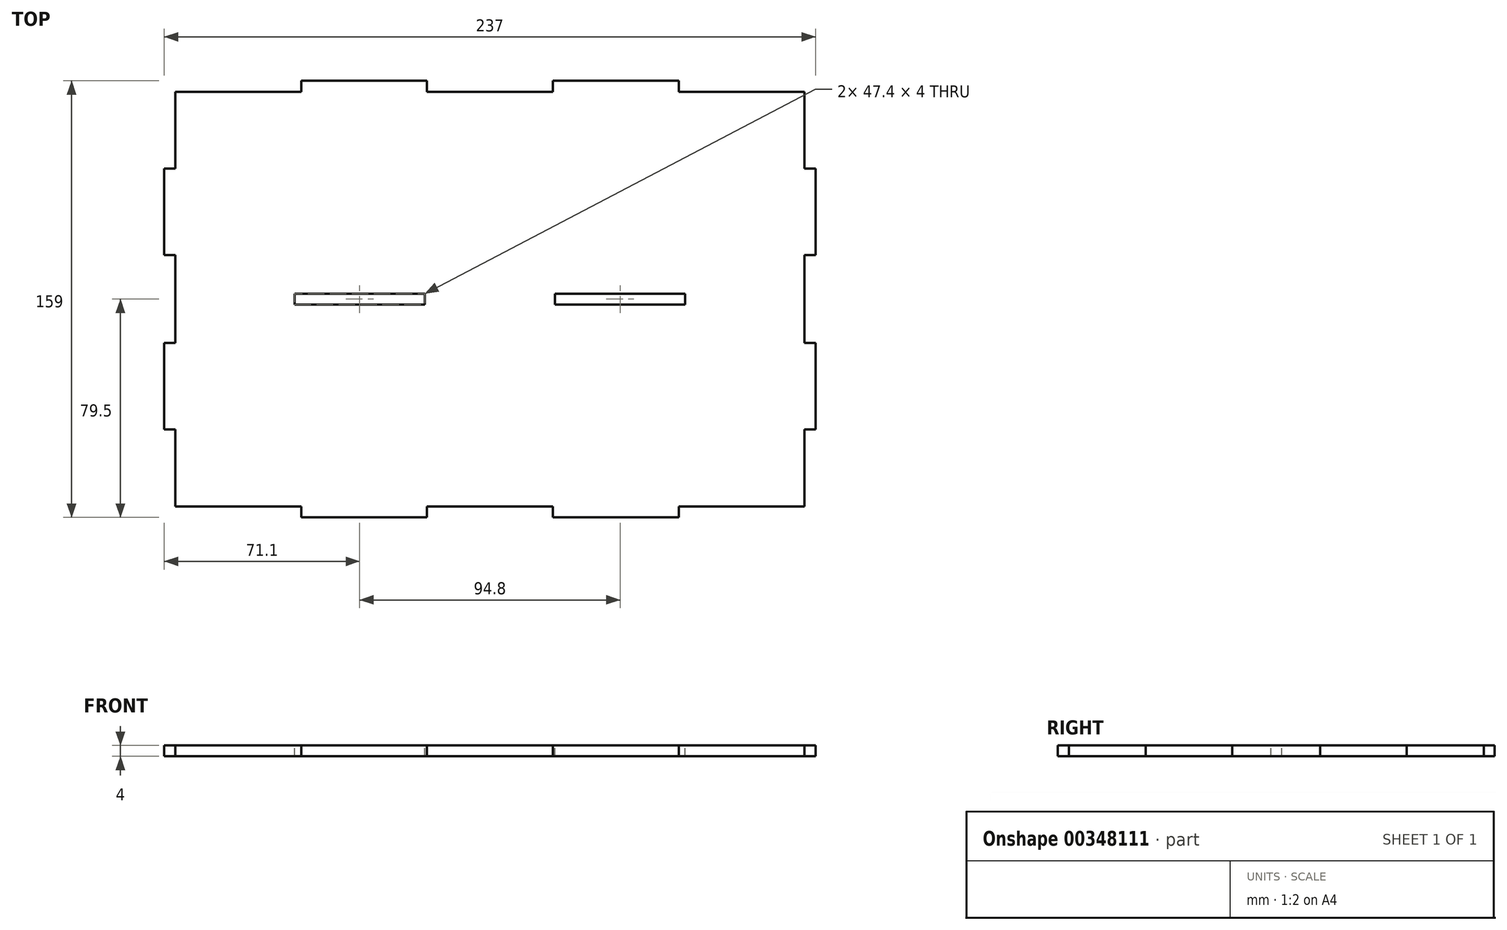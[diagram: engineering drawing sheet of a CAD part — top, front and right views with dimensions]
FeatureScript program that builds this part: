
annotation { "Feature Type Name" : "Feature", "Feature Type Description" : "" }
export const myFeature = defineFeature(function(context is Context, id is Id, definition is map)
    precondition{}
    {
        {
            var Q0;
            Q0=qCreatedBy(makeId("Top.planeOp"),FACE);
            var sketch = newSketch(context, id + "F0", { "sketchPlane" : qUnion([Q0])});
            skLineSegment(sketch, "E0.bottom", {"start": v(0, 0) * mm, "end": v(237, 0) * mm});
            skLineSegment(sketch, "E0.top", {"start": v(0, 159) * mm, "end": v(237, 159) * mm});
            skLineSegment(sketch, "E0.left", {"start": v(0, 0) * mm, "end": v(0, 159) * mm});
            skLineSegment(sketch, "E0.right", {"start": v(237, 0) * mm, "end": v(237, 159) * mm});
            skSolve(sketch);
        }
        {
            var Q0;
            Q0=makeQuery(id+"F0.imprint","IMPRINT",FACE,{"disambiguationData":[TD([[makeQuery(id+"F0.imprint","IMPRINT",EDGE,{"derivedFrom":sQuery(id+"F0.wireOp",EDGE,"E0.bottom")}),1.0]])]});
            extrude(context, id + "F1", {"entities" : qUnion([Q0]), "depth" : 4 * mm});
        }
        {
            var Q0;
            Q0=makeQuery(id+"F1.opExtrude","CAP_FACE",FACE,{"disambiguationData":[OSD([sQuery(id+"F0.wireOp",EDGE,"E0.bottom"),sQuery(id+"F0.wireOp",EDGE,"E0.top"),sQuery(id+"F0.wireOp",EDGE,"E0.left"),sQuery(id+"F0.wireOp",EDGE,"E0.right")])],"isStart":false});
            var sketch = newSketch(context, id + "F2", { "sketchPlane" : qUnion([Q0])});
            skLineSegment(sketch, "E1.0", {"start": v(4, 155) * mm, "end": v(233, 155) * mm, "construction": true});
            skLineSegment(sketch, "E1.1", {"start": v(4, 4) * mm, "end": v(4, 155) * mm, "construction": true});
            skLineSegment(sketch, "E1.2", {"start": v(4, 4) * mm, "end": v(233, 4) * mm, "construction": true});
            skLineSegment(sketch, "E1.3", {"start": v(233, 4) * mm, "end": v(233, 155) * mm, "construction": true});
            skLineSegment(sketch, "E2", {"start": v(4, 79.5) * mm, "end": v(233, 79.5) * mm, "construction": true});
            skLineSegment(sketch, "E3.bottom", {"start": v(4, 32) * mm, "end": v(0, 32) * mm});
            skLineSegment(sketch, "E3.top", {"start": v(4, 0) * mm, "end": v(0, 0) * mm});
            skLineSegment(sketch, "E3.left", {"start": v(4, 32) * mm, "end": v(4, 0) * mm});
            skLineSegment(sketch, "E3.right", {"start": v(0, 32) * mm, "end": v(0, 0) * mm});
            skLineSegment(sketch, "E4.bottom", {"start": v(4, 79.5) * mm, "end": v(0, 79.5) * mm});
            skLineSegment(sketch, "E4.top", {"start": v(4, 63.5) * mm, "end": v(0, 63.5) * mm});
            skLineSegment(sketch, "E4.left", {"start": v(4, 79.5) * mm, "end": v(4, 63.5) * mm});
            skLineSegment(sketch, "E4.right", {"start": v(0, 79.5) * mm, "end": v(0, 63.5) * mm});
            skLineSegment(sketch, "E5", {"start": v(118.5, 4) * mm, "end": v(118.5, 155) * mm, "construction": true});
            skLineSegment(sketch, "E6.MirrorCS", {"start": v(233, 63.5) * mm, "end": v(237, 63.5) * mm});
            skLineSegment(sketch, "E7.MirrorCS", {"start": v(237, 79.5) * mm, "end": v(237, 63.5) * mm});
            skLineSegment(sketch, "E8.MirrorCS", {"start": v(233, 79.5) * mm, "end": v(237, 79.5) * mm});
            skLineSegment(sketch, "E9.MirrorCS", {"start": v(233, 32) * mm, "end": v(237, 32) * mm});
            skLineSegment(sketch, "E10.MirrorCS", {"start": v(237, 32) * mm, "end": v(237, 0) * mm});
            skLineSegment(sketch, "E11.MirrorCS", {"start": v(233, 0) * mm, "end": v(237, 0) * mm});
            skLineSegment(sketch, "E12.MirrorCS", {"start": v(233, 32) * mm, "end": v(233, 0) * mm});
            skLineSegment(sketch, "E13", {"start": v(233, 79.5) * mm, "end": v(233, 63.5) * mm});
            skLineSegment(sketch, "E14.MirrorCS", {"start": v(233, 79.5) * mm, "end": v(233, 95.5) * mm});
            skLineSegment(sketch, "E15.MirrorCS", {"start": v(233, 127) * mm, "end": v(233, 159) * mm});
            skLineSegment(sketch, "E16.MirrorCS", {"start": v(233, 159) * mm, "end": v(237, 159) * mm});
            skLineSegment(sketch, "E17.MirrorCS", {"start": v(233, 127) * mm, "end": v(237, 127) * mm});
            skLineSegment(sketch, "E18.MirrorCS", {"start": v(233, 95.5) * mm, "end": v(237, 95.5) * mm});
            skLineSegment(sketch, "E19.MirrorCS", {"start": v(233, 155) * mm, "end": v(233, 4) * mm, "construction": true});
            skLineSegment(sketch, "E20.MirrorCS", {"start": v(237, 127) * mm, "end": v(237, 159) * mm});
            skLineSegment(sketch, "E21.MirrorCS", {"start": v(237, 79.5) * mm, "end": v(237, 95.5) * mm});
            skLineSegment(sketch, "E22.MirrorCS", {"start": v(4, 159) * mm, "end": v(0, 159) * mm});
            skLineSegment(sketch, "E23.MirrorCS", {"start": v(4, 127) * mm, "end": v(0, 127) * mm});
            skLineSegment(sketch, "E24.MirrorCS", {"start": v(4, 95.5) * mm, "end": v(0, 95.5) * mm});
            skLineSegment(sketch, "E25.MirrorCS", {"start": v(0, 127) * mm, "end": v(0, 159) * mm});
            skLineSegment(sketch, "E26.MirrorCS", {"start": v(4, 127) * mm, "end": v(4, 159) * mm});
            skLineSegment(sketch, "E27.MirrorCS", {"start": v(0, 79.5) * mm, "end": v(0, 95.5) * mm});
            skLineSegment(sketch, "E28.MirrorCS", {"start": v(4, 79.5) * mm, "end": v(4, 95.5) * mm});
            skSolve(sketch);
        }
        {
            var Q0;
            Q0 = qSketchRegion(id + "F2", true);
            extrude(context, id + "F3", {"entities" : qUnion([Q0]), "operationType" : NewBodyOperationType.REMOVE, "endBound" : BoundingType.UP_TO_NEXT, "oppositeDirection" : true, "depth" : 25 * mm});
        }
        {
            var Q0;
            Q0=makeQuery(id+"F1.opExtrude","CAP_FACE",FACE,{"disambiguationData":[OSD([sQuery(id+"F0.wireOp",EDGE,"E0.bottom"),sQuery(id+"F0.wireOp",EDGE,"E0.top"),sQuery(id+"F0.wireOp",EDGE,"E0.left"),sQuery(id+"F0.wireOp",EDGE,"E0.right")])],"isStart":false});
            var sketch = newSketch(context, id + "F4", { "sketchPlane" : qUnion([Q0])});
            skLineSegment(sketch, "E29", {"start": v(4, 79.5) * mm, "end": v(233, 79.5) * mm, "construction": true});
            skLineSegment(sketch, "E30.bottom", {"start": v(4, 0) * mm, "end": v(49.8, 0) * mm});
            skLineSegment(sketch, "E30.top", {"start": v(4, 4) * mm, "end": v(49.8, 4) * mm});
            skLineSegment(sketch, "E30.left", {"start": v(4, 0) * mm, "end": v(4, 4) * mm});
            skLineSegment(sketch, "E30.right", {"start": v(49.8, 0) * mm, "end": v(49.8, 4) * mm});
            skLineSegment(sketch, "E31.bottom", {"start": v(95.6, 0) * mm, "end": v(141.4, 0) * mm});
            skLineSegment(sketch, "E31.top", {"start": v(95.6, 4) * mm, "end": v(141.4, 4) * mm});
            skLineSegment(sketch, "E31.left", {"start": v(95.6, 0) * mm, "end": v(95.6, 4) * mm});
            skLineSegment(sketch, "E31.right", {"start": v(141.4, 0) * mm, "end": v(141.4, 4) * mm});
            skLineSegment(sketch, "E32.bottom", {"start": v(233, 0) * mm, "end": v(187.2, 0) * mm});
            skLineSegment(sketch, "E32.top", {"start": v(233, 4) * mm, "end": v(187.2, 4) * mm});
            skLineSegment(sketch, "E32.left", {"start": v(233, 0) * mm, "end": v(233, 4) * mm});
            skLineSegment(sketch, "E32.right", {"start": v(187.2, 0) * mm, "end": v(187.2, 4) * mm});
            skLineSegment(sketch, "E33.MirrorCS", {"start": v(233, 159) * mm, "end": v(233, 155) * mm});
            skLineSegment(sketch, "E34.MirrorCS", {"start": v(4, 159) * mm, "end": v(4, 155) * mm});
            skLineSegment(sketch, "E35.MirrorCS", {"start": v(187.2, 159) * mm, "end": v(187.2, 155) * mm});
            skLineSegment(sketch, "E36.MirrorCS", {"start": v(141.4, 159) * mm, "end": v(141.4, 155) * mm});
            skLineSegment(sketch, "E37.MirrorCS", {"start": v(95.6, 159) * mm, "end": v(95.6, 155) * mm});
            skLineSegment(sketch, "E38.MirrorCS", {"start": v(49.8, 159) * mm, "end": v(49.8, 155) * mm});
            skLineSegment(sketch, "E39.MirrorCS", {"start": v(233, 155) * mm, "end": v(187.2, 155) * mm});
            skLineSegment(sketch, "E40.MirrorCS", {"start": v(95.6, 155) * mm, "end": v(141.4, 155) * mm});
            skLineSegment(sketch, "E41.MirrorCS", {"start": v(4, 155) * mm, "end": v(49.8, 155) * mm});
            skLineSegment(sketch, "E42.MirrorCS", {"start": v(4, 155) * mm, "end": v(233, 155) * mm, "construction": true});
            skLineSegment(sketch, "E43.MirrorCS", {"start": v(233, 159) * mm, "end": v(187.2, 159) * mm});
            skLineSegment(sketch, "E44.MirrorCS", {"start": v(95.6, 159) * mm, "end": v(141.4, 159) * mm});
            skLineSegment(sketch, "E45.MirrorCS", {"start": v(4, 159) * mm, "end": v(49.8, 159) * mm});
            skLineSegment(sketch, "E46", {"start": v(49.8, 4) * mm, "end": v(95.6, 4) * mm, "construction": true});
            skLineSegment(sketch, "E47", {"start": v(141.4, 4) * mm, "end": v(187.2, 4) * mm, "construction": true});
            skSolve(sketch);
        }
        {
            var Q0;
            Q0 = qSketchRegion(id + "F4", true);
            extrude(context, id + "F5", {"entities" : qUnion([Q0]), "operationType" : NewBodyOperationType.REMOVE, "endBound" : BoundingType.UP_TO_NEXT, "oppositeDirection" : true, "depth" : 25 * mm});
        }
        {
            var Q0;
            Q0=makeQuery(id+"F1.opExtrude","CAP_FACE",FACE,{"disambiguationData":[OSD([sQuery(id+"F0.wireOp",EDGE,"E0.bottom"),sQuery(id+"F0.wireOp",EDGE,"E0.top"),sQuery(id+"F0.wireOp",EDGE,"E0.left"),sQuery(id+"F0.wireOp",EDGE,"E0.right")])],"isStart":false});
            var sketch = newSketch(context, id + "F6", { "sketchPlane" : qUnion([Q0])});
            skLineSegment(sketch, "E48", {"start": v(4, 79.5) * mm, "end": v(233, 79.5) * mm, "construction": true});
            skLineSegment(sketch, "E49.bottom", {"start": v(47.4, 79.5) * mm, "end": v(94.8, 79.5) * mm});
            skLineSegment(sketch, "E49.top", {"start": v(47.4, 81.5) * mm, "end": v(94.8, 81.5) * mm});
            skLineSegment(sketch, "E49.left", {"start": v(47.4, 79.5) * mm, "end": v(47.4, 81.5) * mm});
            skLineSegment(sketch, "E49.right", {"start": v(94.8, 79.5) * mm, "end": v(94.8, 81.5) * mm});
            skLineSegment(sketch, "E50.bottom", {"start": v(142.2, 79.5) * mm, "end": v(189.6, 79.5) * mm});
            skLineSegment(sketch, "E50.top", {"start": v(142.2, 81.5) * mm, "end": v(189.6, 81.5) * mm});
            skLineSegment(sketch, "E50.left", {"start": v(142.2, 79.5) * mm, "end": v(142.2, 81.5) * mm});
            skLineSegment(sketch, "E50.right", {"start": v(189.6, 79.5) * mm, "end": v(189.6, 81.5) * mm});
            skLineSegment(sketch, "E51.MirrorCS", {"start": v(142.2, 79.5) * mm, "end": v(142.2, 77.5) * mm});
            skLineSegment(sketch, "E52.MirrorCS", {"start": v(47.4, 79.5) * mm, "end": v(47.4, 77.5) * mm});
            skLineSegment(sketch, "E53.MirrorCS", {"start": v(94.8, 79.5) * mm, "end": v(94.8, 77.5) * mm});
            skLineSegment(sketch, "E54.MirrorCS", {"start": v(189.6, 79.5) * mm, "end": v(189.6, 77.5) * mm});
            skLineSegment(sketch, "E55.MirrorCS", {"start": v(142.2, 77.5) * mm, "end": v(189.6, 77.5) * mm});
            skLineSegment(sketch, "E56.MirrorCS", {"start": v(47.4, 77.5) * mm, "end": v(94.8, 77.5) * mm});
            skSolve(sketch);
        }
        {
            var Q0;
            Q0 = qSketchRegion(id + "F6", true);
            extrude(context, id + "F7", {"entities" : qUnion([Q0]), "operationType" : NewBodyOperationType.REMOVE, "endBound" : BoundingType.UP_TO_NEXT, "oppositeDirection" : true, "depth" : 3 * mm});
        }
    });
